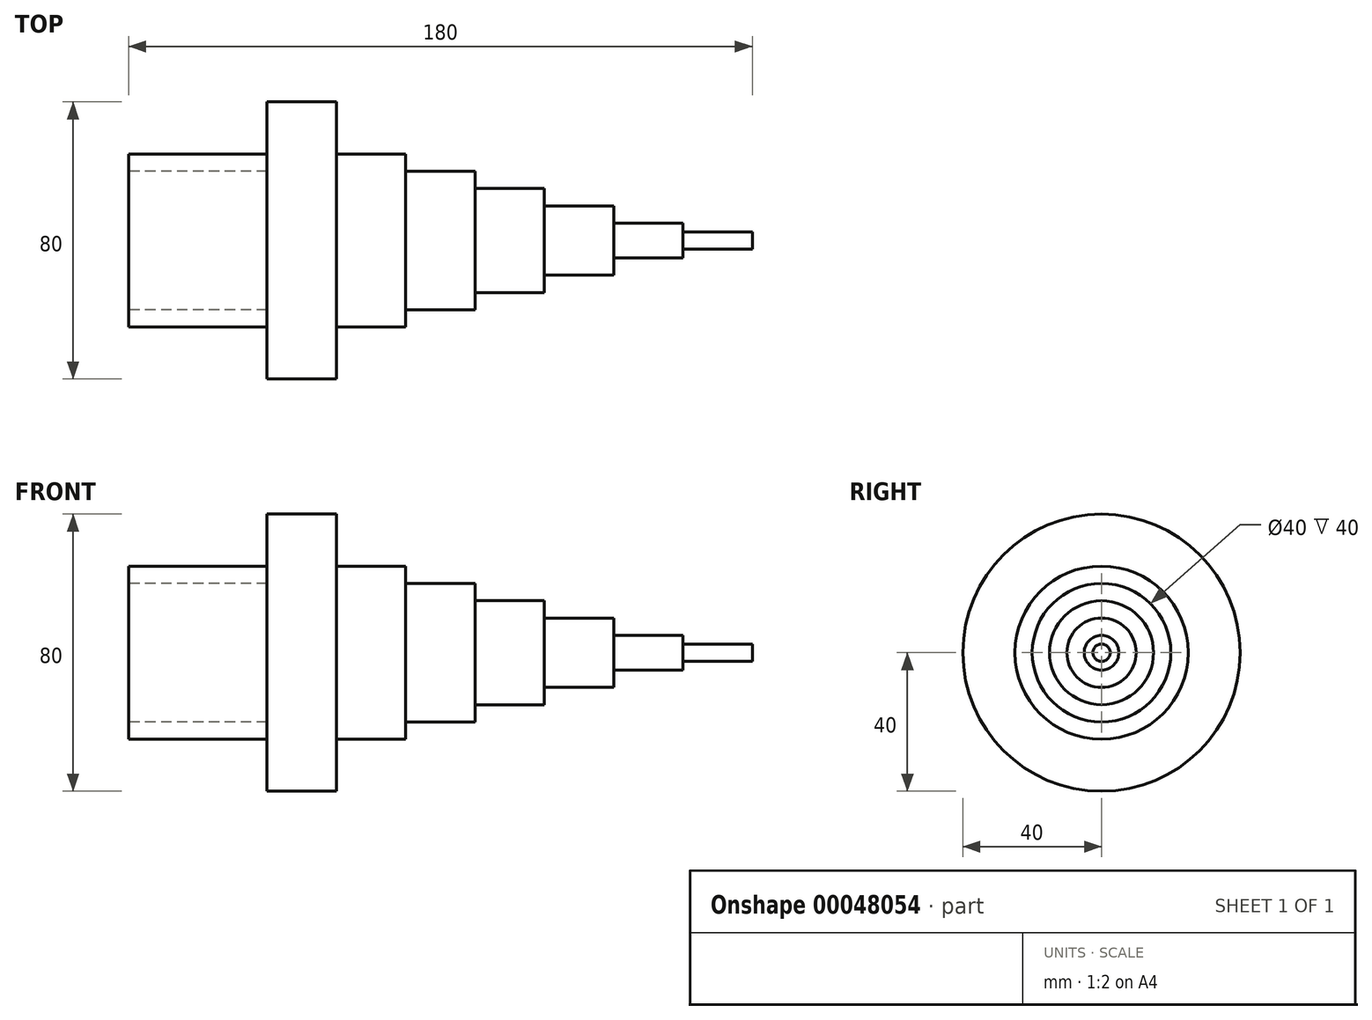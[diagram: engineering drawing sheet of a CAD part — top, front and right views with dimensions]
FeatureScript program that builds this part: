
annotation { "Feature Type Name" : "Feature", "Feature Type Description" : "" }
export const myFeature = defineFeature(function(context is Context, id is Id, definition is map)
    precondition{}
    {
        {
            var Q0;
            Q0=qCreatedBy(makeId("Front.planeOp"),FACE);
            var sketch = newSketch(context, id + "F0", { "sketchPlane" : qUnion([Q0])});
            skLineSegment(sketch, "E0.bottom", {"start": v(0, 0) * mm, "end": v(40, 0) * mm});
            skLineSegment(sketch, "E0.top", {"start": v(0, 50) * mm, "end": v(40, 50) * mm});
            skLineSegment(sketch, "E0.left", {"start": v(0, 0) * mm, "end": v(0, 50) * mm});
            skLineSegment(sketch, "E0.right", {"start": v(40, 0) * mm, "end": v(40, 50) * mm});
            skPoint(sketch, "E1.firstSnap0", {"position": v(40, 25) * mm});
            skLineSegment(sketch, "E1.bottom", {"start": v(40, -15) * mm, "end": v(60, -15) * mm});
            skLineSegment(sketch, "E1.top", {"start": v(40, 65) * mm, "end": v(60, 65) * mm});
            skLineSegment(sketch, "E1.left", {"start": v(40, -15) * mm, "end": v(40, 65) * mm});
            skLineSegment(sketch, "E1.right", {"start": v(60, -15) * mm, "end": v(60, 65) * mm});
            skLineSegment(sketch, "E2.bottom", {"start": v(60, 50) * mm, "end": v(80, 50) * mm});
            skLineSegment(sketch, "E2.top", {"start": v(60, 0) * mm, "end": v(80, 0) * mm});
            skLineSegment(sketch, "E2.left", {"start": v(60, 50) * mm, "end": v(60, 0) * mm});
            skLineSegment(sketch, "E2.right", {"start": v(80, 50) * mm, "end": v(80, 0) * mm});
            skLineSegment(sketch, "E3.bottom", {"start": v(80, 5) * mm, "end": v(100, 5) * mm});
            skLineSegment(sketch, "E3.top", {"start": v(80, 45) * mm, "end": v(100, 45) * mm});
            skLineSegment(sketch, "E3.left", {"start": v(80, 5) * mm, "end": v(80, 45) * mm});
            skLineSegment(sketch, "E3.right", {"start": v(100, 5) * mm, "end": v(100, 45) * mm});
            skLineSegment(sketch, "E4.bottom", {"start": v(100, 40) * mm, "end": v(120, 40) * mm});
            skLineSegment(sketch, "E4.top", {"start": v(100, 10) * mm, "end": v(120, 10) * mm});
            skLineSegment(sketch, "E4.left", {"start": v(100, 40) * mm, "end": v(100, 10) * mm});
            skLineSegment(sketch, "E4.right", {"start": v(120, 40) * mm, "end": v(120, 10) * mm});
            skLineSegment(sketch, "E5.bottom", {"start": v(120, 15) * mm, "end": v(140, 15) * mm});
            skLineSegment(sketch, "E5.top", {"start": v(120, 35) * mm, "end": v(140, 35) * mm});
            skLineSegment(sketch, "E5.left", {"start": v(120, 15) * mm, "end": v(120, 35) * mm});
            skLineSegment(sketch, "E5.right", {"start": v(140, 15) * mm, "end": v(140, 35) * mm});
            skLineSegment(sketch, "E6.bottom", {"start": v(140, 30) * mm, "end": v(160, 30) * mm});
            skLineSegment(sketch, "E6.top", {"start": v(140, 20) * mm, "end": v(160, 20) * mm});
            skLineSegment(sketch, "E6.left", {"start": v(140, 30) * mm, "end": v(140, 20) * mm});
            skLineSegment(sketch, "E6.right", {"start": v(160, 30) * mm, "end": v(160, 20) * mm});
            skLineSegment(sketch, "E7.bottom", {"start": v(160, 27.5) * mm, "end": v(180, 27.5) * mm});
            skLineSegment(sketch, "E7.top", {"start": v(160, 22.5) * mm, "end": v(180, 22.5) * mm});
            skLineSegment(sketch, "E7.left", {"start": v(160, 27.5) * mm, "end": v(160, 22.5) * mm});
            skLineSegment(sketch, "E7.right", {"start": v(180, 27.5) * mm, "end": v(180, 22.5) * mm});
            skLineSegment(sketch, "E8", {"start": v(0, 25) * mm, "end": v(180, 25) * mm});
            skPoint(sketch, "E8.endSnap0", {"position": v(80, 25) * mm});
            skLineSegment(sketch, "E9", {"start": v(0, 45) * mm, "end": v(40, 45) * mm});
            skLineSegment(sketch, "E10", {"start": v(0, 5) * mm, "end": v(40, 5) * mm});
            skPoint(sketch, "E11", {"position": v(160, 25) * mm});
            skPoint(sketch, "E12", {"position": v(140, 25) * mm});
            skPoint(sketch, "E13", {"position": v(120, 25) * mm});
            skPoint(sketch, "E14", {"position": v(100, 25) * mm});
            skSolve(sketch);
        }
        {
            var Q0;
            {var subQ2=sQuery(id+"F0.wireOp",EDGE,"E0.top");Q0=makeQuery(id+"F0.imprint","IMPRINT",FACE,{"disambiguationData":[TD([[makeQuery(id+"F0.imprint","IMPRINT",EDGE,{"derivedFrom":subQ2}),-1.0]])]});}
            var Q1;
            {var subQ7=sQuery(id+"F0.wireOp",EDGE,"E1.top");Q1=makeQuery(id+"F0.imprint","IMPRINT",FACE,{"disambiguationData":[TD([[makeQuery(id+"F0.imprint","IMPRINT",EDGE,{"derivedFrom":subQ7}),-1.0]])]});}
            var Q2;
            {var subQ5=sQuery(id+"F0.wireOp",EDGE,"E2.bottom");Q2=makeQuery(id+"F0.imprint","IMPRINT",FACE,{"disambiguationData":[TD([[makeQuery(id+"F0.imprint","IMPRINT",EDGE,{"derivedFrom":subQ5}),-1.0]])]});}
            var Q3;
            {var subQ0=sQuery(id+"F0.wireOp",EDGE,"E3.top");Q3=makeQuery(id+"F0.imprint","IMPRINT",FACE,{"disambiguationData":[TD([[makeQuery(id+"F0.imprint","IMPRINT",EDGE,{"derivedFrom":subQ0}),-1.0]])]});}
            var Q4;
            {var subQ5=sQuery(id+"F0.wireOp",EDGE,"E4.bottom");Q4=makeQuery(id+"F0.imprint","IMPRINT",FACE,{"disambiguationData":[TD([[makeQuery(id+"F0.imprint","IMPRINT",EDGE,{"derivedFrom":subQ5}),-1.0]])]});}
            var Q5;
            {var subQ5=sQuery(id+"F0.wireOp",EDGE,"E5.top");Q5=makeQuery(id+"F0.imprint","IMPRINT",FACE,{"disambiguationData":[TD([[makeQuery(id+"F0.imprint","IMPRINT",EDGE,{"derivedFrom":subQ5}),-1.0]])]});}
            var Q6;
            {var subQ5=sQuery(id+"F0.wireOp",EDGE,"E6.bottom");Q6=makeQuery(id+"F0.imprint","IMPRINT",FACE,{"disambiguationData":[TD([[makeQuery(id+"F0.imprint","IMPRINT",EDGE,{"derivedFrom":subQ5}),-1.0]])]});}
            var Q7;
            {var subQ5=sQuery(id+"F0.wireOp",EDGE,"E7.bottom");Q7=makeQuery(id+"F0.imprint","IMPRINT",FACE,{"disambiguationData":[TD([[makeQuery(id+"F0.imprint","IMPRINT",EDGE,{"derivedFrom":subQ5}),-1.0]])]});}
            var Q8;
            Q8=sQuery(id+"F0.wireOp",EDGE,"E8");
            revolve(context, id + "F1", {"entities" : qUnion([Q0, Q1, Q2, Q3, Q4, Q5, Q6, Q7]), "axis" : qUnion([Q8]), "revolveType" : RevolveType.FULL});
        }
    });
